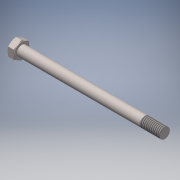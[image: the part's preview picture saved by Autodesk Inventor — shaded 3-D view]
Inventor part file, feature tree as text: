
AUTODESK INVENTOR PART (.ipt)
format: ipt  version: 2016 (Build 200138000, 138)  size: 136,192 bytes
history: native  units: in
note: dims shown in document units (in); Inventor stores cm internally (conversion verified against a paired STEP export)
features: extrude x2, sketch x2, thread x1, projected_geometry x1, other x1
ambient origin geometry x8: Origin, YZ Plane, XZ Plane, XY Plane, X Axis, Y Axis, Z Axis, Center Point
bodies: Solid1 (feature_tree)
feature tree (7):
  extrude  "Extrusion1"  Depth=1.047in TaperAngle=0.0deg
  extrude  "Extrusion2"  [1 undecoded]
  thread  "Thread1"  [1 undecoded]
  sketch  "Sketch1"  dims[d0=0.04in d1=0.0in d2=1.047in d3=0.0in]
  sketch  "Sketch2"  dims[d4=1.0in d5=0.0in]
  projected_geometry  "Projected Loop1"
  other  "HeadFillet"
note: 2 required parameter values undecoded (feature->parameter linkage not recoverable at this tier; creation-order binding heuristic only, values carry confidence <= 0.55)
